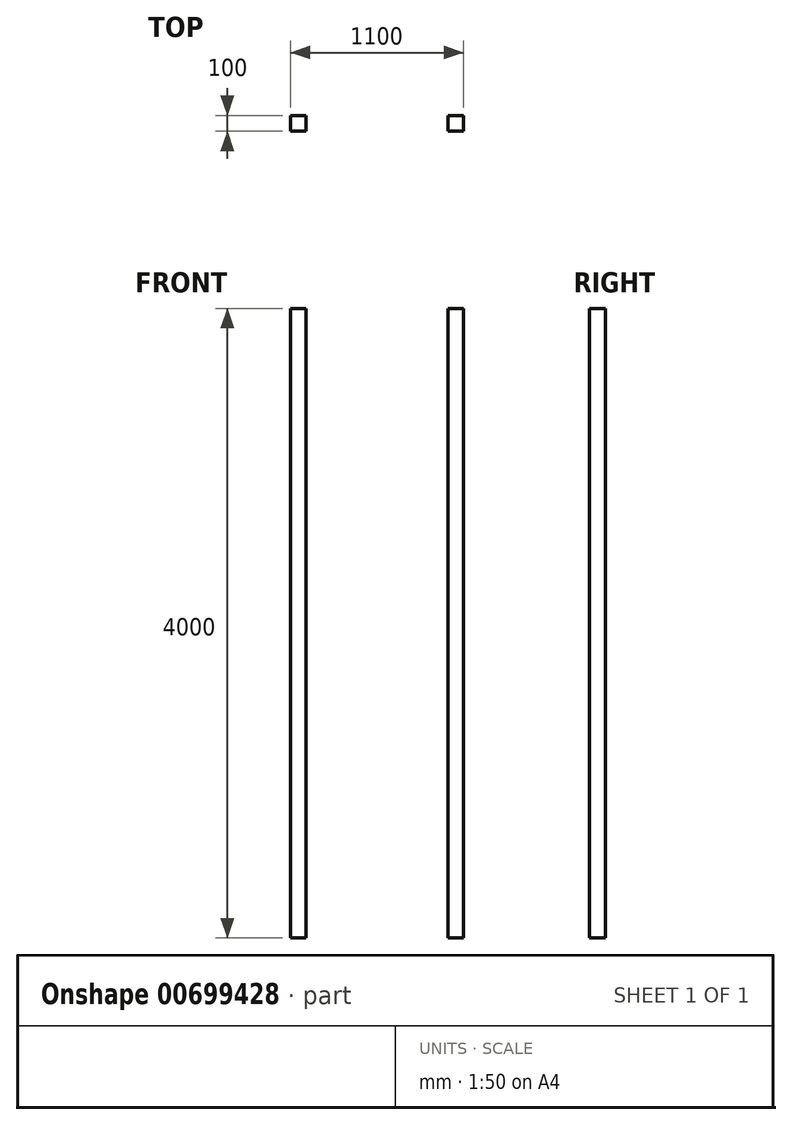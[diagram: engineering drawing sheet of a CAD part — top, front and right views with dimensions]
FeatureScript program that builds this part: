
annotation { "Feature Type Name" : "Feature", "Feature Type Description" : "" }
export const myFeature = defineFeature(function(context is Context, id is Id, definition is map)
    precondition{}
    {
        {
            var Q0;
            Q0=qCreatedBy(makeId("Front.planeOp"),FACE);
            var sketch = newSketch(context, id + "F0", { "sketchPlane" : qUnion([Q0])});
            skLineSegment(sketch, "E0.bottom", {"start": v(-46.95, 3989.88) * mm, "end": v(53.05, 3989.88) * mm});
            skLineSegment(sketch, "E0.top", {"start": v(-46.95, -10.12) * mm, "end": v(53.05, -10.12) * mm});
            skLineSegment(sketch, "E0.left", {"start": v(-46.95, 3989.88) * mm, "end": v(-46.95, -10.12) * mm});
            skLineSegment(sketch, "E0.right", {"start": v(53.05, 3989.88) * mm, "end": v(53.05, -10.12) * mm});
            skSolve(sketch);
        }
        {
            var Q0;
            Q0=makeQuery(id+"F0.imprint","IMPRINT",FACE,{"disambiguationData":[TD([[makeQuery(id+"F0.imprint","IMPRINT",EDGE,{"derivedFrom":sQuery(id+"F0.wireOp",EDGE,"E0.bottom")}),-1.0]])]});
            extrude(context, id + "F1", {"entities" : qUnion([Q0]), "depth" : 100 * mm, "offsetDistance" : 25 * mm});
        }
        {
            var Q0;
            Q0=makeQuery(id+"F1.opExtrude","SWEPT_BODY",BODY,{"disambiguationData":[OSD([sQuery(id+"F0.wireOp",EDGE,"E0.bottom"),sQuery(id+"F0.wireOp",EDGE,"E0.top"),sQuery(id+"F0.wireOp",EDGE,"E0.left"),sQuery(id+"F0.wireOp",EDGE,"E0.right")])]});
            transform(context, id + "F2", {"entities" : qUnion([Q0]), "transformType" : TransformType.TRANSLATION_3D, "dx" : 1000 * mm, "dy" : 0 * mm, "dz" : 0 * mm, "makeCopy" : true});
        }
    });
